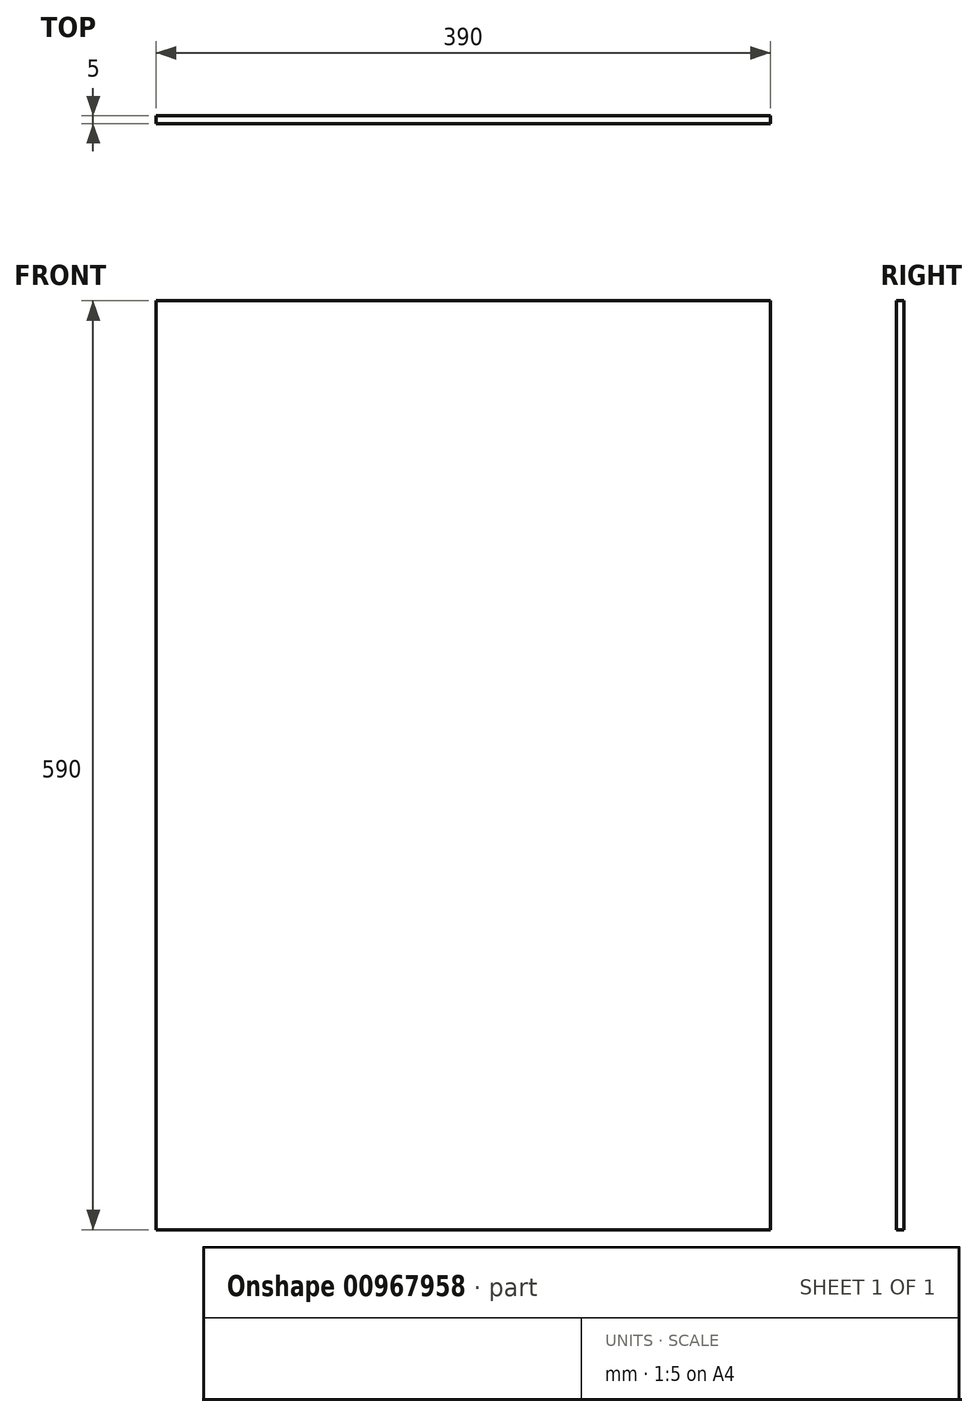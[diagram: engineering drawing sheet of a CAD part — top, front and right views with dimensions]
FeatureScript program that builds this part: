
annotation { "Feature Type Name" : "Feature", "Feature Type Description" : "" }
export const myFeature = defineFeature(function(context is Context, id is Id, definition is map)
    precondition{}
    {
        {
            var Q0;
            Q0=qCreatedBy(makeId("Front.planeOp"),FACE);
            var sketch = newSketch(context, id + "F0", { "sketchPlane" : qUnion([Q0])});
            skLineSegment(sketch, "E0.bottom", {"start": v(195, -295) * mm, "end": v(-195, -295) * mm});
            skLineSegment(sketch, "E0.top", {"start": v(195, 295) * mm, "end": v(-195, 295) * mm});
            skLineSegment(sketch, "E0.left", {"start": v(195, -295) * mm, "end": v(195, 295) * mm});
            skLineSegment(sketch, "E0.right", {"start": v(-195, -295) * mm, "end": v(-195, 295) * mm});
            skPoint(sketch, "E0.middle", {"position": v(0, 0) * mm});
            skSolve(sketch);
        }
        {
            var Q0;
            Q0 = qSketchRegion(id + "F0", true);
            extrude(context, id + "F1", {"entities" : qUnion([Q0]), "depth" : 5 * mm, "offsetDistance" : 25 * mm});
        }
    });
